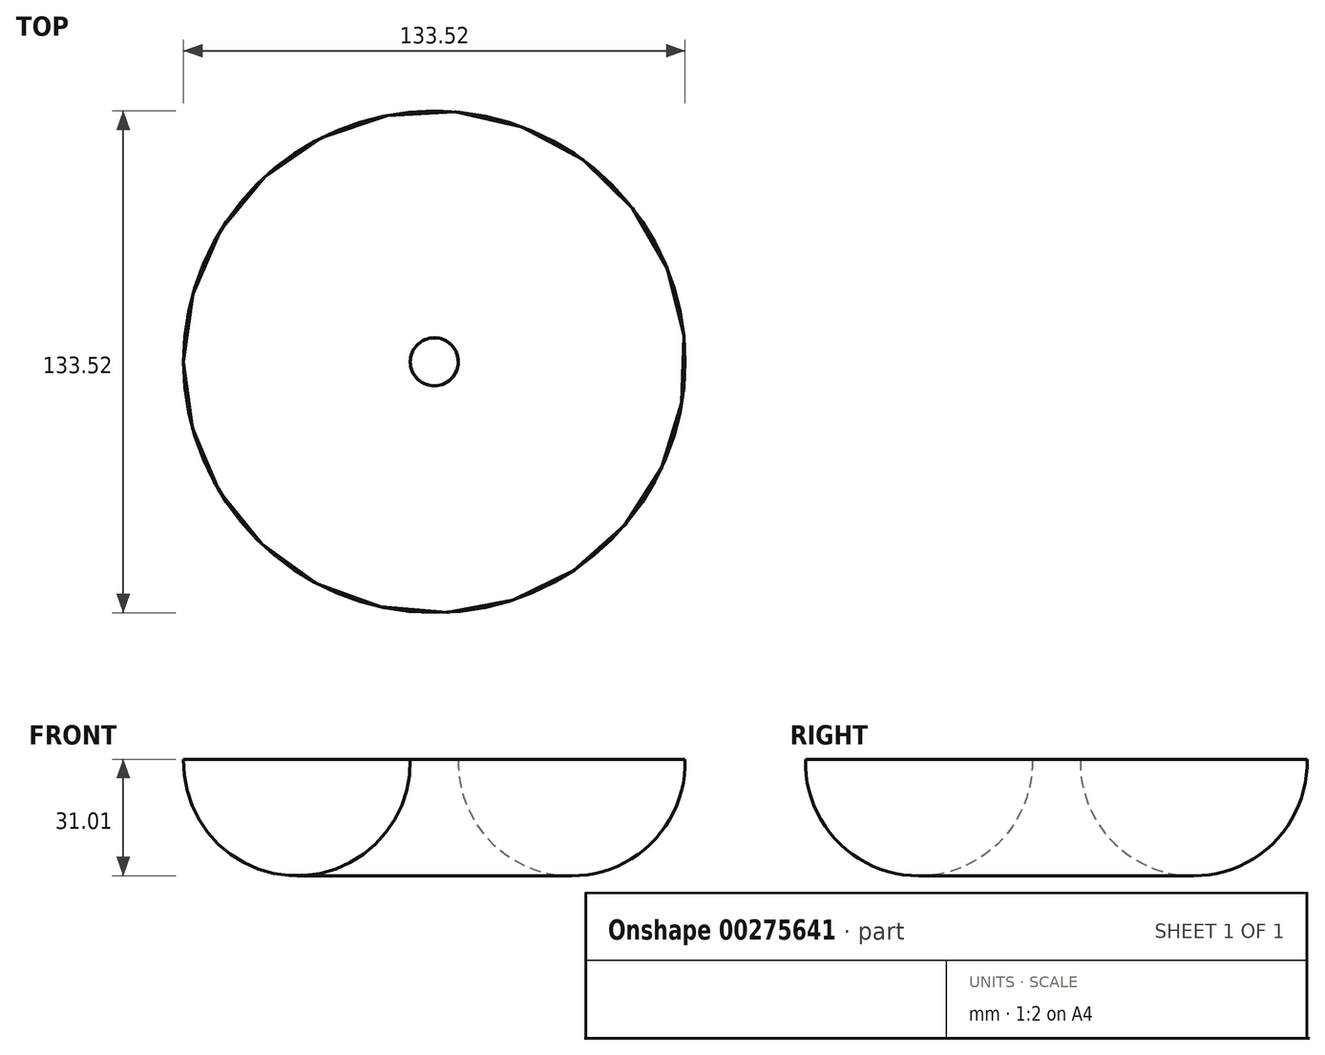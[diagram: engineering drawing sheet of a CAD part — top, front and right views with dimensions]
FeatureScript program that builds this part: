
annotation { "Feature Type Name" : "Feature", "Feature Type Description" : "" }
export const myFeature = defineFeature(function(context is Context, id is Id, definition is map)
    precondition{}
    {
        {
            var Q0;
            Q0=qCreatedBy(makeId("Right.planeOp"),FACE);
            var sketch = newSketch(context, id + "F0", { "sketchPlane" : qUnion([Q0])});
            skArc(sketch, "E0", {"start": v(6.41, 0) * mm, "mid": v(36.58, -31.01) * mm, "end": v(66.75, 0) * mm});
            skLineSegment(sketch, "E1", {"start": v(0, 67.19) * mm, "end": v(0, -58.44) * mm, "construction": true});
            skSolve(sketch);
        }
        {
            var Q0;
            Q0=sQuery(id+"F0.wireOp",EDGE,"E0");
            var Q1;
            Q1=sQuery(id+"F0.wireOp",EDGE,"E1");
            revolve(context, id + "F1", {"bodyType" : ToolBodyType.SURFACE, "surfaceEntities" : qUnion([Q0]), "axis" : qUnion([Q1]), "revolveType" : RevolveType.FULL});
        }
    });
